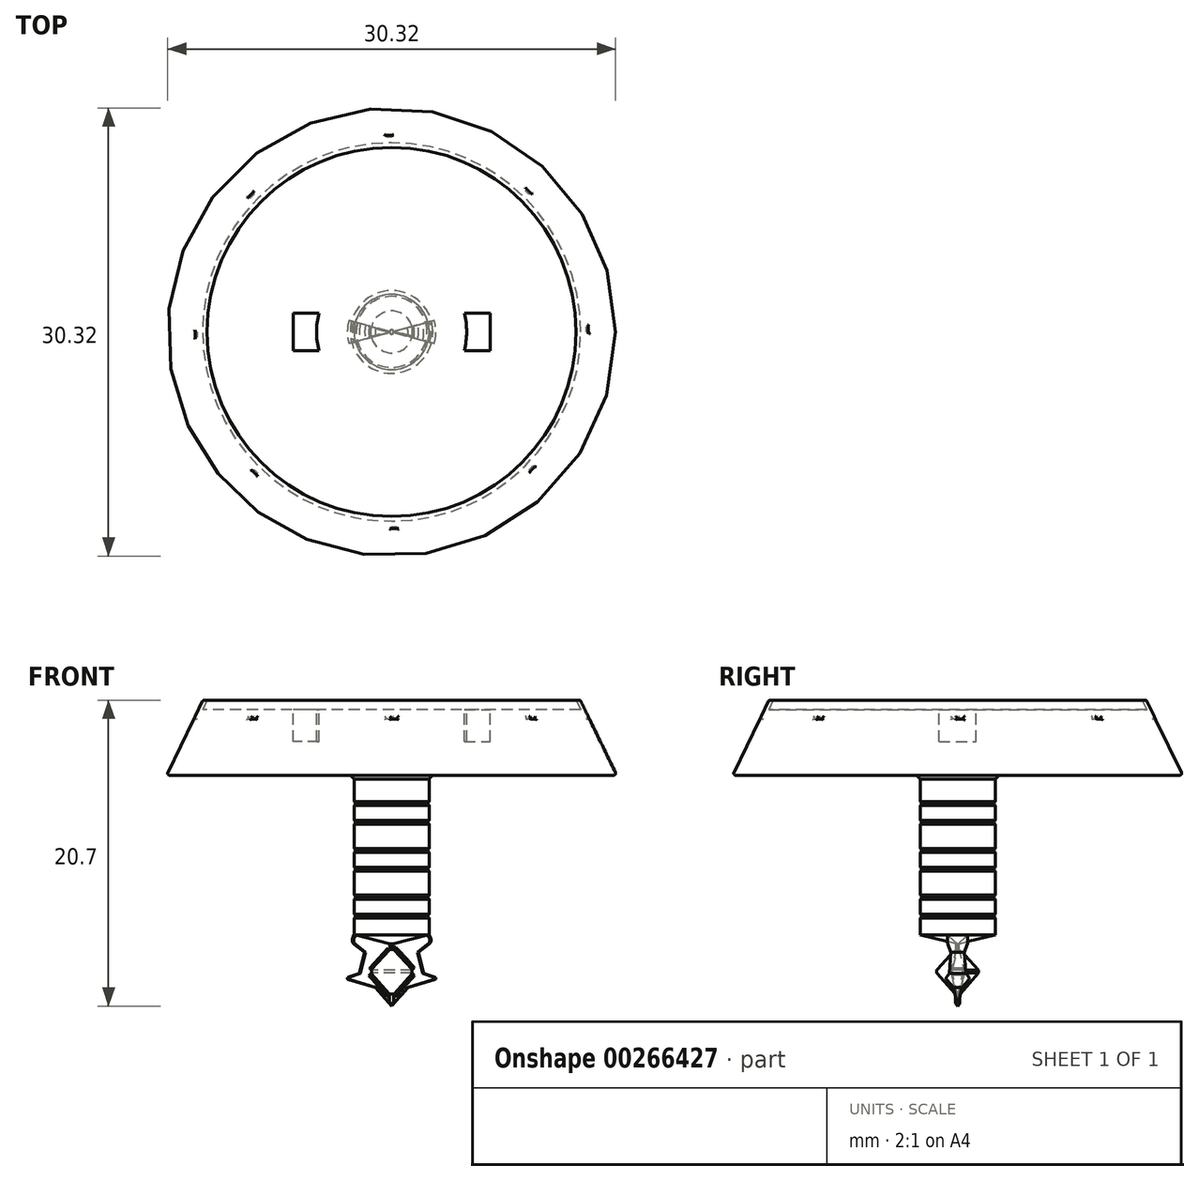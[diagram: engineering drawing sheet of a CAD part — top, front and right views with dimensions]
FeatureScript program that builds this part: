
annotation { "Feature Type Name" : "Feature", "Feature Type Description" : "" }
export const myFeature = defineFeature(function(context is Context, id is Id, definition is map)
    precondition{}
    {
        {
            var Q0;
            Q0=qCreatedBy(makeId("Top.planeOp"),FACE);
            var sketch = newSketch(context, id + "F0", { "sketchPlane" : qUnion([Q0])});
            skLineSegment(sketch, "E0", {"start": v(-1.59, 0) * mm, "end": v(-1.59, 1.27) * mm});
            skLineSegment(sketch, "E1", {"start": v(1.59, 0) * mm, "end": v(1.59, 1.27) * mm});
            skLineSegment(sketch, "E2", {"start": v(1.59, 0) * mm, "end": v(1.59, -1.27) * mm});
            skLineSegment(sketch, "E3", {"start": v(-1.59, 0) * mm, "end": v(-1.59, -1.27) * mm});
            skLineSegment(sketch, "E4.bottom", {"start": v(1.59, -1.27) * mm, "end": v(6.67, -1.27) * mm});
            skLineSegment(sketch, "E4.top", {"start": v(1.59, 1.26) * mm, "end": v(6.67, 1.26) * mm});
            skLineSegment(sketch, "E4.left", {"start": v(1.59, -1.27) * mm, "end": v(1.59, 1.26) * mm});
            skLineSegment(sketch, "E4.right", {"start": v(6.67, -1.27) * mm, "end": v(6.67, 1.26) * mm});
            skLineSegment(sketch, "E5.bottom", {"start": v(-1.59, -1.27) * mm, "end": v(-6.67, -1.27) * mm});
            skLineSegment(sketch, "E5.top", {"start": v(-1.59, 1.26) * mm, "end": v(-6.67, 1.26) * mm});
            skLineSegment(sketch, "E5.left", {"start": v(-1.59, -1.27) * mm, "end": v(-1.59, 1.26) * mm});
            skLineSegment(sketch, "E5.right", {"start": v(-6.67, -1.27) * mm, "end": v(-6.67, 1.26) * mm});
            skCircle(sketch, "E6", {"center": v(0, 0) * mm, "radius": 5.08 * mm});
            skCircle(sketch, "E7", {"center": v(0, 0) * mm, "radius": 12.7 * mm});
            skLineSegment(sketch, "E8", {"start": v(0, 0) * mm, "end": v(-1.59, 0) * mm});
            skLineSegment(sketch, "E9", {"start": v(0, 0) * mm, "end": v(1.59, 0) * mm});
            skSolve(sketch);
        }
        {
            var Q0;
            Q0=qCreatedBy(makeId("Front.planeOp"),FACE);
            var sketch = newSketch(context, id + "F1", { "sketchPlane" : qUnion([Q0])});
            skLineSegment(sketch, "E10", {"start": v(0, 0) * mm, "end": v(0, -1.27) * mm});
            skLineSegment(sketch, "E11", {"start": v(0, -1.27) * mm, "end": v(0, -3.81) * mm});
            skLineSegment(sketch, "E12", {"start": v(0, -3.81) * mm, "end": v(0, -5.08) * mm});
            skLineSegment(sketch, "E13", {"start": v(0, -5.08) * mm, "end": v(0, -6.99) * mm});
            skLineSegment(sketch, "E14", {"start": v(0, -14.6) * mm, "end": v(0, -16.51) * mm});
            skLineSegment(sketch, "E15", {"start": v(0.24, -16.76) * mm, "end": v(1.54, -18.15) * mm});
            skLineSegment(sketch, "E16", {"start": v(1.54, -18.58) * mm, "end": v(0.26, -20.03) * mm});
            skLineSegment(sketch, "E17", {"start": v(0, -16.98) * mm, "end": v(0, -19.74) * mm});
            skLineSegment(sketch, "E18", {"start": v(2.18, -18.5) * mm, "end": v(3.18, -18.84) * mm});
            skLineSegment(sketch, "E19", {"start": v(0.12, -16.48) * mm, "end": v(2.54, -15.9) * mm});
            skLineSegment(sketch, "E20", {"start": v(0.12, -16.5) * mm, "end": v(2.79, -16.33) * mm});
            skLineSegment(sketch, "E21", {"start": v(0.12, -16.55) * mm, "end": v(1.82, -17.06) * mm});
            skLineSegment(sketch, "E22", {"start": v(1.82, -17.06) * mm, "end": v(2.79, -16.33) * mm});
            skLineSegment(sketch, "E23", {"start": v(1.82, -17.06) * mm, "end": v(2.18, -18.5) * mm});
            skLineSegment(sketch, "E24", {"start": v(0, -5.08) * mm, "end": v(14.96, -5.08) * mm});
            skLineSegment(sketch, "E25", {"start": v(12.49, 0) * mm, "end": v(0, 0) * mm});
            skLineSegment(sketch, "E26", {"start": v(0, -1.27) * mm, "end": v(13.1, -1.27) * mm});
            skLineSegment(sketch, "E27", {"start": v(0, -3.81) * mm, "end": v(14.34, -3.81) * mm});
            skLineSegment(sketch, "E28.MirrorCS", {"start": v(0, -1.27) * mm, "end": v(-13.39, -1.27) * mm});
            skLineSegment(sketch, "E29.MirrorCS", {"start": v(0, -3.81) * mm, "end": v(-14.62, -3.81) * mm});
            skLineSegment(sketch, "E30.MirrorCS", {"start": v(0, -5.08) * mm, "end": v(-15.24, -5.08) * mm});
            skLineSegment(sketch, "E31.MirrorCS", {"start": v(-15.24, -5.08) * mm, "end": v(-12.77, 0) * mm});
            skLineSegment(sketch, "E32.MirrorCS", {"start": v(-12.77, 0) * mm, "end": v(0, 0) * mm});
            skLineSegment(sketch, "E33", {"start": v(0, 0) * mm, "end": v(2.54, 0) * mm});
            skLineSegment(sketch, "E34", {"start": v(2.54, -15.9) * mm, "end": v(2.79, -16.33) * mm});
            skLineSegment(sketch, "E35", {"start": v(0, -6.99) * mm, "end": v(2.4, -6.99) * mm});
            skLineSegment(sketch, "E36", {"start": v(0, -10.16) * mm, "end": v(2.4, -10.16) * mm});
            skLineSegment(sketch, "E37", {"start": v(0, -11.43) * mm, "end": v(2.4, -11.43) * mm});
            skLineSegment(sketch, "E38", {"start": v(0, -13.33) * mm, "end": v(2.4, -13.33) * mm});
            skLineSegment(sketch, "E39", {"start": v(0, -14.6) * mm, "end": v(2.4, -14.6) * mm});
            skLineSegment(sketch, "E40", {"start": v(2.54, -15.9) * mm, "end": v(2.54, -14.73) * mm});
            skLineSegment(sketch, "E41", {"start": v(2.54, -14.48) * mm, "end": v(2.54, -13.46) * mm});
            skLineSegment(sketch, "E42", {"start": v(2.54, -13.2) * mm, "end": v(2.54, -11.56) * mm});
            skLineSegment(sketch, "E43", {"start": v(2.54, -11.3) * mm, "end": v(2.54, -10.29) * mm});
            skLineSegment(sketch, "E44", {"start": v(2.54, -10.03) * mm, "end": v(2.54, -8.38) * mm});
            skLineSegment(sketch, "E45", {"start": v(2.54, -8.13) * mm, "end": v(2.54, -7.11) * mm});
            skLineSegment(sketch, "E46", {"start": v(2.54, -6.86) * mm, "end": v(2.54, -5.33) * mm});
            skLineSegment(sketch, "E47.MirrorCS", {"start": v(-0.12, -16.48) * mm, "end": v(-2.54, -15.9) * mm});
            skLineSegment(sketch, "E48.MirrorCS", {"start": v(-0.12, -16.5) * mm, "end": v(-2.79, -16.33) * mm});
            skLineSegment(sketch, "E49.MirrorCS", {"start": v(-0.12, -16.55) * mm, "end": v(-1.82, -17.06) * mm});
            skLineSegment(sketch, "E50.MirrorCS", {"start": v(-1.82, -17.06) * mm, "end": v(-2.79, -16.33) * mm});
            skLineSegment(sketch, "E51.MirrorCS", {"start": v(-2.54, -15.9) * mm, "end": v(-2.79, -16.33) * mm});
            skLineSegment(sketch, "E52.0", {"start": v(1.11, -19.45) * mm, "end": v(0, -20.7) * mm});
            skLineSegment(sketch, "E53", {"start": v(3.18, -18.84) * mm, "end": v(1.11, -19.45) * mm});
            skLineSegment(sketch, "E54", {"start": v(0, -5.08) * mm, "end": v(0, -5.33) * mm});
            skLineSegment(sketch, "E55", {"start": v(0, -5.33) * mm, "end": v(2.54, -5.33) * mm});
            skLineSegment(sketch, "E56", {"start": v(0, -6.86) * mm, "end": v(2.54, -6.86) * mm});
            skLineSegment(sketch, "E57", {"start": v(0, -7.11) * mm, "end": v(2.54, -7.11) * mm});
            skLineSegment(sketch, "E58", {"start": v(0, -8.13) * mm, "end": v(2.54, -8.13) * mm});
            skLineSegment(sketch, "E59", {"start": v(0, -8.38) * mm, "end": v(2.54, -8.38) * mm});
            skLineSegment(sketch, "E60", {"start": v(0, -10.03) * mm, "end": v(2.54, -10.03) * mm});
            skLineSegment(sketch, "E61", {"start": v(0, -10.29) * mm, "end": v(2.54, -10.29) * mm});
            skLineSegment(sketch, "E62", {"start": v(0, -11.3) * mm, "end": v(2.54, -11.3) * mm});
            skLineSegment(sketch, "E63", {"start": v(0, -11.56) * mm, "end": v(2.54, -11.56) * mm});
            skLineSegment(sketch, "E64", {"start": v(0, -13.2) * mm, "end": v(2.54, -13.2) * mm});
            skLineSegment(sketch, "E65", {"start": v(0, -13.46) * mm, "end": v(2.54, -13.46) * mm});
            skLineSegment(sketch, "E66", {"start": v(0, -14.48) * mm, "end": v(2.54, -14.48) * mm});
            skLineSegment(sketch, "E67", {"start": v(0, -14.73) * mm, "end": v(2.54, -14.73) * mm});
            skLineSegment(sketch, "E68", {"start": v(0, -5.08) * mm, "end": v(2.8, -5.08) * mm});
            skLineSegment(sketch, "E69", {"start": v(2.54, -5.33) * mm, "end": v(2.8, -5.08) * mm});
            skPoint(sketch, "E70.orphan", {"position": v(2.54, -5.08) * mm});
            skLineSegment(sketch, "E71", {"start": v(2.4, -6.99) * mm, "end": v(2.54, -6.86) * mm});
            skLineSegment(sketch, "E72", {"start": v(2.54, -7.11) * mm, "end": v(2.4, -6.98) * mm});
            skLineSegment(sketch, "E73", {"start": v(2.4, -8.26) * mm, "end": v(2.54, -8.13) * mm});
            skLineSegment(sketch, "E74", {"start": v(2.4, -8.26) * mm, "end": v(2.54, -8.38) * mm});
            skLineSegment(sketch, "E75", {"start": v(2.4, -10.16) * mm, "end": v(2.54, -10.03) * mm});
            skLineSegment(sketch, "E76", {"start": v(2.54, -10.29) * mm, "end": v(2.4, -10.16) * mm});
            skLineSegment(sketch, "E77", {"start": v(2.4, -11.43) * mm, "end": v(2.54, -11.3) * mm});
            skLineSegment(sketch, "E78", {"start": v(2.54, -11.56) * mm, "end": v(2.4, -11.43) * mm});
            skLineSegment(sketch, "E79", {"start": v(2.4, -13.34) * mm, "end": v(2.54, -13.2) * mm});
            skLineSegment(sketch, "E80", {"start": v(2.54, -13.46) * mm, "end": v(2.4, -13.33) * mm});
            skLineSegment(sketch, "E81", {"start": v(2.4, -14.6) * mm, "end": v(2.54, -14.48) * mm});
            skLineSegment(sketch, "E82", {"start": v(2.54, -14.73) * mm, "end": v(2.4, -14.6) * mm});
            skPoint(sketch, "E83.orphan", {"position": v(2.54, -6.99) * mm});
            skPoint(sketch, "E84.orphan", {"position": v(2.54, -8.26) * mm});
            skPoint(sketch, "E85.start.orphan", {"position": v(2.54, -10.16) * mm});
            skPoint(sketch, "E86.start.orphan", {"position": v(2.54, -11.43) * mm});
            skPoint(sketch, "E87.orphan", {"position": v(2.54, -14.6) * mm});
            skPoint(sketch, "E88.orphan", {"position": v(2.54, -13.33) * mm});
            skLineSegment(sketch, "E89", {"start": v(0, -6.86) * mm, "end": v(0, -14.73) * mm});
            skLineSegment(sketch, "E90.MirrorCS", {"start": v(0, -14.73) * mm, "end": v(-2.54, -14.73) * mm});
            skLineSegment(sketch, "E91.MirrorCS", {"start": v(-2.54, -15.9) * mm, "end": v(-2.54, -14.73) * mm});
            skLineSegment(sketch, "E92.MirrorCS", {"start": v(-2.54, -14.73) * mm, "end": v(-2.4, -14.6) * mm});
            skLineSegment(sketch, "E93.MirrorCS", {"start": v(-2.4, -10.16) * mm, "end": v(-2.54, -10.03) * mm});
            skLineSegment(sketch, "E94.MirrorCS", {"start": v(-2.4, -11.43) * mm, "end": v(-2.54, -11.3) * mm});
            skLineSegment(sketch, "E95.MirrorCS", {"start": v(-2.54, -11.56) * mm, "end": v(-2.4, -11.43) * mm});
            skLineSegment(sketch, "E96.MirrorCS", {"start": v(-2.4, -14.6) * mm, "end": v(-2.54, -14.48) * mm});
            skLineSegment(sketch, "E97.MirrorCS", {"start": v(-2.4, -8.26) * mm, "end": v(-2.54, -8.38) * mm});
            skLineSegment(sketch, "E98.MirrorCS", {"start": v(-2.4, -6.99) * mm, "end": v(-2.54, -6.86) * mm});
            skLineSegment(sketch, "E99.MirrorCS", {"start": v(-2.54, -13.46) * mm, "end": v(-2.4, -13.33) * mm});
            skLineSegment(sketch, "E100.MirrorCS", {"start": v(-2.4, -8.26) * mm, "end": v(-2.54, -8.13) * mm});
            skLineSegment(sketch, "E101.MirrorCS", {"start": v(-2.54, -7.11) * mm, "end": v(-2.4, -6.98) * mm});
            skLineSegment(sketch, "E102.MirrorCS", {"start": v(-2.4, -13.34) * mm, "end": v(-2.54, -13.2) * mm});
            skLineSegment(sketch, "E103.MirrorCS", {"start": v(-2.54, -10.29) * mm, "end": v(-2.4, -10.16) * mm});
            skLineSegment(sketch, "E104.MirrorCS", {"start": v(-2.54, -5.33) * mm, "end": v(-2.8, -5.08) * mm});
            skLineSegment(sketch, "E105.MirrorCS", {"start": v(0, -7.11) * mm, "end": v(-2.54, -7.11) * mm});
            skPoint(sketch, "E106.MirrorP", {"position": v(-2.54, -10.16) * mm});
            skLineSegment(sketch, "E107.MirrorCS", {"start": v(-2.54, -11.3) * mm, "end": v(-2.54, -10.29) * mm});
            skLineSegment(sketch, "E108.MirrorCS", {"start": v(0, -10.03) * mm, "end": v(-2.54, -10.03) * mm});
            skPoint(sketch, "E109.MirrorP", {"position": v(-2.54, -6.99) * mm});
            skLineSegment(sketch, "E110.MirrorCS", {"start": v(0, -8.38) * mm, "end": v(-2.54, -8.38) * mm});
            skLineSegment(sketch, "E111.MirrorCS", {"start": v(0, -11.3) * mm, "end": v(-2.54, -11.3) * mm});
            skLineSegment(sketch, "E112.MirrorCS", {"start": v(0, -6.86) * mm, "end": v(-2.54, -6.86) * mm});
            skLineSegment(sketch, "E113.MirrorCS", {"start": v(0, -13.46) * mm, "end": v(-2.54, -13.46) * mm});
            skLineSegment(sketch, "E114.MirrorCS", {"start": v(0, -5.08) * mm, "end": v(-2.8, -5.08) * mm});
            skLineSegment(sketch, "E115.MirrorCS", {"start": v(0, -14.48) * mm, "end": v(-2.54, -14.48) * mm});
            skLineSegment(sketch, "E116.MirrorCS", {"start": v(0, -10.16) * mm, "end": v(-2.4, -10.16) * mm});
            skPoint(sketch, "E117.MirrorP", {"position": v(-2.54, -11.43) * mm});
            skPoint(sketch, "E118.MirrorP", {"position": v(-2.54, -13.33) * mm});
            skPoint(sketch, "E119.MirrorP", {"position": v(-2.54, -5.08) * mm});
            skLineSegment(sketch, "E120.MirrorCS", {"start": v(0, -13.2) * mm, "end": v(-2.54, -13.2) * mm});
            skLineSegment(sketch, "E121.MirrorCS", {"start": v(-2.54, -10.03) * mm, "end": v(-2.54, -8.38) * mm});
            skPoint(sketch, "E122.MirrorP", {"position": v(-2.54, -8.26) * mm});
            skLineSegment(sketch, "E123.MirrorCS", {"start": v(0, -8.13) * mm, "end": v(-2.54, -8.13) * mm});
            skPoint(sketch, "E124.MirrorP", {"position": v(-2.54, -14.6) * mm});
            skLineSegment(sketch, "E125.MirrorCS", {"start": v(0, -14.6) * mm, "end": v(-2.4, -14.6) * mm});
            skLineSegment(sketch, "E126.MirrorCS", {"start": v(-2.54, -6.86) * mm, "end": v(-2.54, -5.33) * mm});
            skLineSegment(sketch, "E127.MirrorCS", {"start": v(0, -11.56) * mm, "end": v(-2.54, -11.56) * mm});
            skLineSegment(sketch, "E128.MirrorCS", {"start": v(0, -13.33) * mm, "end": v(-2.4, -13.33) * mm});
            skLineSegment(sketch, "E129.MirrorCS", {"start": v(0, -5.33) * mm, "end": v(-2.54, -5.33) * mm});
            skLineSegment(sketch, "E130.MirrorCS", {"start": v(-2.54, -14.48) * mm, "end": v(-2.54, -13.46) * mm});
            skLineSegment(sketch, "E131.MirrorCS", {"start": v(0, -11.43) * mm, "end": v(-2.4, -11.43) * mm});
            skLineSegment(sketch, "E132.MirrorCS", {"start": v(0, -10.29) * mm, "end": v(-2.54, -10.29) * mm});
            skLineSegment(sketch, "E133.MirrorCS", {"start": v(0, -6.99) * mm, "end": v(-2.4, -6.99) * mm});
            skLineSegment(sketch, "E134.MirrorCS", {"start": v(-2.54, -8.13) * mm, "end": v(-2.54, -7.11) * mm});
            skLineSegment(sketch, "E135.MirrorCS", {"start": v(-2.54, -13.2) * mm, "end": v(-2.54, -11.56) * mm});
            skLineSegment(sketch, "E136", {"start": v(-2.4, -8.26) * mm, "end": v(2.4, -8.26) * mm});
            skLineSegment(sketch, "E137", {"start": v(0, 0) * mm, "end": v(0, -0.64) * mm});
            skLineSegment(sketch, "E138", {"start": v(0, -0.64) * mm, "end": v(12.8, -0.64) * mm});
            skLineSegment(sketch, "E139", {"start": v(0, -0.64) * mm, "end": v(-13.08, -0.64) * mm});
            skLineSegment(sketch, "E140.0", {"start": v(-14.96, -5.08) * mm, "end": v(-12.49, 0) * mm});
            skLineSegment(sketch, "E141", {"start": v(0.24, -16.76) * mm, "end": v(0.12, -16.87) * mm});
            skLineSegment(sketch, "E142", {"start": v(0.26, -20.03) * mm, "end": v(0.15, -19.9) * mm});
            skLineSegment(sketch, "E143", {"start": v(1.42, -18.47) * mm, "end": v(1.54, -18.58) * mm});
            skLineSegment(sketch, "E144.MirrorCS", {"start": v(1.42, -18.26) * mm, "end": v(1.54, -18.15) * mm});
            skLineSegment(sketch, "E145", {"start": v(1.42, -18.47) * mm, "end": v(0.15, -19.9) * mm});
            skLineSegment(sketch, "E146", {"start": v(1.42, -18.26) * mm, "end": v(0.12, -16.87) * mm});
            skPoint(sketch, "E146.endSnap0", {"position": v(0.12, -16.87) * mm});
            skLineSegment(sketch, "E147", {"start": v(0, -0.64) * mm, "end": v(0, -3.81) * mm});
            skLineSegment(sketch, "E148.MirrorCS", {"start": v(14.96, -5.08) * mm, "end": v(12.49, 0) * mm});
            skPoint(sketch, "E149.orphan", {"position": v(12.77, 0) * mm});
            skPoint(sketch, "E150.orphan", {"position": v(13.39, -1.27) * mm});
            skPoint(sketch, "E151.orphan", {"position": v(14.62, -3.81) * mm});
            skPoint(sketch, "E152.orphan", {"position": v(15.24, -5.08) * mm});
            skLineSegment(sketch, "E153", {"start": v(1.42, -18.47) * mm, "end": v(1.42, -18.26) * mm});
            skLineSegment(sketch, "E154", {"start": v(0, -16.98) * mm, "end": v(0, -16.51) * mm});
            skLineSegment(sketch, "E155", {"start": v(0, -19.74) * mm, "end": v(0, -20.7) * mm});
            skLineSegment(sketch, "E156.MirrorCS", {"start": v(-1.42, -18.26) * mm, "end": v(-0.12, -16.87) * mm});
            skLineSegment(sketch, "E157.MirrorCS", {"start": v(-0.24, -16.76) * mm, "end": v(-0.12, -16.87) * mm});
            skLineSegment(sketch, "E158.MirrorCS", {"start": v(-0.24, -16.76) * mm, "end": v(-1.54, -18.15) * mm});
            skLineSegment(sketch, "E159.MirrorCS", {"start": v(-1.42, -18.47) * mm, "end": v(-1.54, -18.58) * mm});
            skLineSegment(sketch, "E160.MirrorCS", {"start": v(-1.42, -18.26) * mm, "end": v(-1.54, -18.15) * mm});
            skLineSegment(sketch, "E161.MirrorCS", {"start": v(-1.42, -18.47) * mm, "end": v(-0.15, -19.9) * mm});
            skLineSegment(sketch, "E162.MirrorCS", {"start": v(-1.11, -19.45) * mm, "end": v(0, -20.7) * mm});
            skLineSegment(sketch, "E163.MirrorCS", {"start": v(-1.42, -18.47) * mm, "end": v(-1.42, -18.26) * mm});
            skLineSegment(sketch, "E164.MirrorCS", {"start": v(-3.18, -18.84) * mm, "end": v(-1.11, -19.45) * mm});
            skLineSegment(sketch, "E165.MirrorCS", {"start": v(-1.82, -17.06) * mm, "end": v(-2.18, -18.5) * mm});
            skLineSegment(sketch, "E166.MirrorCS", {"start": v(-2.18, -18.5) * mm, "end": v(-3.18, -18.84) * mm});
            skLineSegment(sketch, "E167.MirrorCS", {"start": v(-1.54, -18.58) * mm, "end": v(-0.26, -20.03) * mm});
            skLineSegment(sketch, "E168.MirrorCS", {"start": v(-0.26, -20.03) * mm, "end": v(-0.15, -19.9) * mm});
            skPoint(sketch, "E169.orphan", {"position": v(-0.12, -16.86) * mm});
            skPoint(sketch, "E170.orphan", {"position": v(0.12, -16.86) * mm});
            skLineSegment(sketch, "E171", {"start": v(0.12, -16.87) * mm, "end": v(0.12, -16.48) * mm});
            skLineSegment(sketch, "E172", {"start": v(0.12, -16.48) * mm, "end": v(-0.12, -16.48) * mm});
            skLineSegment(sketch, "E173", {"start": v(-0.12, -16.48) * mm, "end": v(-0.12, -16.87) * mm});
            skPoint(sketch, "E174.orphan", {"position": v(0, -16.98) * mm});
            skLineSegment(sketch, "E175", {"start": v(-0.15, -19.9) * mm, "end": v(-0.15, -20.54) * mm});
            skLineSegment(sketch, "E176", {"start": v(0.15, -20.54) * mm, "end": v(0.15, -19.9) * mm});
            skPoint(sketch, "E177.orphan", {"position": v(0, -19.74) * mm});
            skSolve(sketch);
        }
        {
            var Q0;
            {var subQ0=sQuery(id+"F1.wireOp",EDGE,"E137");Q0=makeQuery(id+"F1.imprint","IMPRINT",FACE,{"disambiguationData":[TD([[makeQuery(id+"F1.imprint","IMPRINT",EDGE,{"derivedFrom":subQ0}),-1.0]])]});}
            var Q1;
            {var subQ0=sQuery(id+"F1.wireOp",EDGE,"E28.MirrorCS");var subQ1=sQuery(id+"F1.wireOp",EDGE,"E140.0");var subQ2=makeQuery(id+"F1.imprint","INTERSECT",VERTEX,{"derivedFrom":[subQ1,subQ0]});Q1=makeQuery(id+"F1.imprint","IMPRINT",FACE,{"disambiguationData":[TD([[makeQuery(id+"F1.imprint","IMPRINT",EDGE,{"disambiguationData":[TD([[subQ2,-1.0]])],"derivedFrom":subQ1}),-1.0]])]});}
            var Q2;
            {var subQ0=sQuery(id+"F1.wireOp",EDGE,"E29.MirrorCS");var subQ1=sQuery(id+"F1.wireOp",EDGE,"E140.0");var subQ2=makeQuery(id+"F1.imprint","INTERSECT",VERTEX,{"derivedFrom":[subQ1,subQ0]});Q2=makeQuery(id+"F1.imprint","IMPRINT",FACE,{"disambiguationData":[TD([[makeQuery(id+"F1.imprint","IMPRINT",EDGE,{"disambiguationData":[TD([[subQ2,-1.0]])],"derivedFrom":subQ1}),-1.0]])]});}
            var Q3;
            {var subQ6=sQuery(id+"F1.wireOp",EDGE,"E12");Q3=makeQuery(id+"F1.imprint","IMPRINT",FACE,{"disambiguationData":[TD([[makeQuery(id+"F1.imprint","IMPRINT",EDGE,{"derivedFrom":subQ6}),-1.0]])]});}
            var Q4;
            Q4=makeQuery(id+"F1.imprint","IMPRINT",FACE,{"disambiguationData":[TD([[makeQuery(id+"F1.imprint","IMPRINT",EDGE,{"derivedFrom":sQuery(id+"F1.wireOp",EDGE,"E104.MirrorCS")}),-1.0]])]});
            var Q5;
            {var subQ2=sQuery(id+"F1.wireOp",EDGE,"E112.MirrorCS");Q5=makeQuery(id+"F1.imprint","IMPRINT",FACE,{"disambiguationData":[TD([[makeQuery(id+"F1.imprint","IMPRINT",EDGE,{"derivedFrom":subQ2}),-1.0]])]});}
            var Q6;
            Q6=makeQuery(id+"F1.imprint","IMPRINT",FACE,{"disambiguationData":[TD([[makeQuery(id+"F1.imprint","IMPRINT",EDGE,{"derivedFrom":sQuery(id+"F1.wireOp",EDGE,"E98.MirrorCS")}),-1.0]])]});
            var Q7;
            Q7=makeQuery(id+"F1.imprint","IMPRINT",FACE,{"disambiguationData":[TD([[makeQuery(id+"F1.imprint","IMPRINT",EDGE,{"derivedFrom":sQuery(id+"F1.wireOp",EDGE,"E101.MirrorCS")}),-1.0]])]});
            var Q8;
            {var subQ0=sQuery(id+"F1.wireOp",EDGE,"E105.MirrorCS");Q8=makeQuery(id+"F1.imprint","IMPRINT",FACE,{"disambiguationData":[TD([[makeQuery(id+"F1.imprint","IMPRINT",EDGE,{"derivedFrom":subQ0}),1.0]])]});}
            var Q9;
            {var subQ4=sQuery(id+"F1.wireOp",EDGE,"E100.MirrorCS");Q9=makeQuery(id+"F1.imprint","IMPRINT",FACE,{"disambiguationData":[TD([[makeQuery(id+"F1.imprint","IMPRINT",EDGE,{"derivedFrom":subQ4}),-1.0]])]});}
            var Q10;
            {var subQ2=sQuery(id+"F1.wireOp",EDGE,"E108.MirrorCS");Q10=makeQuery(id+"F1.imprint","IMPRINT",FACE,{"disambiguationData":[TD([[makeQuery(id+"F1.imprint","IMPRINT",EDGE,{"derivedFrom":subQ2}),-1.0]])]});}
            var Q11;
            {var subQ4=sQuery(id+"F1.wireOp",EDGE,"E97.MirrorCS");Q11=makeQuery(id+"F1.imprint","IMPRINT",FACE,{"disambiguationData":[TD([[makeQuery(id+"F1.imprint","IMPRINT",EDGE,{"derivedFrom":subQ4}),1.0]])]});}
            var Q12;
            Q12=makeQuery(id+"F1.imprint","IMPRINT",FACE,{"disambiguationData":[TD([[makeQuery(id+"F1.imprint","IMPRINT",EDGE,{"derivedFrom":sQuery(id+"F1.wireOp",EDGE,"E103.MirrorCS")}),-1.0]])]});
            var Q13;
            Q13=makeQuery(id+"F1.imprint","IMPRINT",FACE,{"disambiguationData":[TD([[makeQuery(id+"F1.imprint","IMPRINT",EDGE,{"derivedFrom":sQuery(id+"F1.wireOp",EDGE,"E93.MirrorCS")}),-1.0]])]});
            var Q14;
            Q14=makeQuery(id+"F1.imprint","IMPRINT",FACE,{"disambiguationData":[TD([[makeQuery(id+"F1.imprint","IMPRINT",EDGE,{"derivedFrom":sQuery(id+"F1.wireOp",EDGE,"E107.MirrorCS")}),-1.0]])]});
            var Q15;
            Q15=makeQuery(id+"F1.imprint","IMPRINT",FACE,{"disambiguationData":[TD([[makeQuery(id+"F1.imprint","IMPRINT",EDGE,{"derivedFrom":sQuery(id+"F1.wireOp",EDGE,"E94.MirrorCS")}),-1.0]])]});
            var Q16;
            Q16=makeQuery(id+"F1.imprint","IMPRINT",FACE,{"disambiguationData":[TD([[makeQuery(id+"F1.imprint","IMPRINT",EDGE,{"derivedFrom":sQuery(id+"F1.wireOp",EDGE,"E95.MirrorCS")}),-1.0]])]});
            var Q17;
            {var subQ2=sQuery(id+"F1.wireOp",EDGE,"E120.MirrorCS");Q17=makeQuery(id+"F1.imprint","IMPRINT",FACE,{"disambiguationData":[TD([[makeQuery(id+"F1.imprint","IMPRINT",EDGE,{"derivedFrom":subQ2}),-1.0]])]});}
            var Q18;
            Q18=makeQuery(id+"F1.imprint","IMPRINT",FACE,{"disambiguationData":[TD([[makeQuery(id+"F1.imprint","IMPRINT",EDGE,{"derivedFrom":sQuery(id+"F1.wireOp",EDGE,"E102.MirrorCS")}),-1.0]])]});
            var Q19;
            Q19=makeQuery(id+"F1.imprint","IMPRINT",FACE,{"disambiguationData":[TD([[makeQuery(id+"F1.imprint","IMPRINT",EDGE,{"derivedFrom":sQuery(id+"F1.wireOp",EDGE,"E99.MirrorCS")}),-1.0]])]});
            var Q20;
            {var subQ0=sQuery(id+"F1.wireOp",EDGE,"E113.MirrorCS");Q20=makeQuery(id+"F1.imprint","IMPRINT",FACE,{"disambiguationData":[TD([[makeQuery(id+"F1.imprint","IMPRINT",EDGE,{"derivedFrom":subQ0}),1.0]])]});}
            var Q21;
            Q21=makeQuery(id+"F1.imprint","IMPRINT",FACE,{"disambiguationData":[TD([[makeQuery(id+"F1.imprint","IMPRINT",EDGE,{"derivedFrom":sQuery(id+"F1.wireOp",EDGE,"E96.MirrorCS")}),-1.0]])]});
            var Q22;
            {var subQ0=sQuery(id+"F1.wireOp",EDGE,"E90.MirrorCS");Q22=makeQuery(id+"F1.imprint","IMPRINT",FACE,{"disambiguationData":[TD([[makeQuery(id+"F1.imprint","IMPRINT",EDGE,{"derivedFrom":subQ0}),-1.0]])]});}
            var Q23;
            {var subQ0=sQuery(id+"F1.wireOp",EDGE,"E47.MirrorCS");Q23=makeQuery(id+"F1.imprint","IMPRINT",FACE,{"disambiguationData":[TD([[makeQuery(id+"F1.imprint","IMPRINT",EDGE,{"derivedFrom":subQ0}),-1.0]])]});}
            var Q24;
            Q24=sQuery(id+"F1.wireOp",EDGE,"E14");
            revolve(context, id + "F2", {"entities" : qUnion([Q0, Q1, Q2, Q3, Q4, Q5, Q6, Q7, Q8, Q9, Q10, Q11, Q12, Q13, Q14, Q15, Q16, Q17, Q18, Q19, Q20, Q21, Q22, Q23]), "axis" : qUnion([Q24]), "revolveType" : RevolveType.FULL});
        }
        {
            var Q0;
            {var subQ2=sQuery(id+"F1.wireOp",EDGE,"E17");Q0=makeQuery(id+"F1.imprint","IMPRINT",FACE,{"disambiguationData":[TD([[makeQuery(id+"F1.imprint","IMPRINT",EDGE,{"derivedFrom":subQ2}),1.0]])]});}
            var Q1;
            Q1=sQuery(id+"F1.wireOp",EDGE,"E17");
            revolve(context, id + "F3", {"entities" : qUnion([Q0]), "axis" : qUnion([Q1]), "revolveType" : RevolveType.FULL});
        }
        {
            var Q0;
            {var subQ0=sQuery(id+"F1.wireOp",EDGE,"E32.MirrorCS");var subQ1=sQuery(id+"F1.wireOp",EDGE,"E31.MirrorCS");var subQ2=makeQuery(id+"F1.imprint","INTERSECT",VERTEX,{"derivedFrom":[subQ1,subQ0]});Q0=makeQuery(id+"F1.imprint","IMPRINT",FACE,{"disambiguationData":[TD([[makeQuery(id+"F1.imprint","IMPRINT",EDGE,{"disambiguationData":[TD([[subQ2,1.0]])],"derivedFrom":subQ1}),-1.0]])]});}
            var Q1;
            Q1=sQuery(id+"F1.wireOp",EDGE,"E137");
            revolve(context, id + "F4", {"operationType" : NewBodyOperationType.ADD, "entities" : qUnion([Q0]), "axis" : qUnion([Q1]), "revolveType" : RevolveType.FULL});
        }
        {
            var Q0;
            {var subQ0=sQuery(id+"F1.wireOp",EDGE,"E28.MirrorCS");var subQ1=sQuery(id+"F1.wireOp",EDGE,"E31.MirrorCS");var subQ2=makeQuery(id+"F1.imprint","INTERSECT",VERTEX,{"derivedFrom":[subQ1,subQ0]});Q0=makeQuery(id+"F1.imprint","IMPRINT",FACE,{"disambiguationData":[TD([[makeQuery(id+"F1.imprint","IMPRINT",EDGE,{"disambiguationData":[TD([[subQ2,-1.0]])],"derivedFrom":subQ1}),-1.0]])]});}
            var Q1;
            Q1=sQuery(id+"F1.wireOp",EDGE,"E10");
            revolve(context, id + "F5", {"entities" : qUnion([Q0]), "axis" : qUnion([Q1]), "revolveType" : RevolveType.SYMMETRIC, "angle" : 43.5 * degree});
        }
        {
            var Q0;
            {var subQ0=sQuery(id+"F1.wireOp",EDGE,"E29.MirrorCS");var subQ1=sQuery(id+"F1.wireOp",EDGE,"E31.MirrorCS");var subQ2=makeQuery(id+"F1.imprint","INTERSECT",VERTEX,{"derivedFrom":[subQ1,subQ0]});Q0=makeQuery(id+"F1.imprint","IMPRINT",FACE,{"disambiguationData":[TD([[makeQuery(id+"F1.imprint","IMPRINT",EDGE,{"disambiguationData":[TD([[subQ2,-1.0]])],"derivedFrom":subQ1}),-1.0]])]});}
            var Q1;
            Q1=sQuery(id+"F1.wireOp",EDGE,"E11");
            revolve(context, id + "F6", {"entities" : qUnion([Q0]), "axis" : qUnion([Q1]), "revolveType" : RevolveType.ONE_DIRECTION, "angle" : 43.5 * degree});
        }
        {
            var Q0;
            {var subQ0=sQuery(id+"F1.wireOp",EDGE,"E31.MirrorCS");var subQ1=sQuery(id+"F1.wireOp",EDGE,"E30.MirrorCS");var subQ2=makeQuery(id+"F1.imprint","INTERSECT",VERTEX,{"derivedFrom":[subQ1,subQ0]});Q0=makeQuery(id+"F1.imprint","IMPRINT",FACE,{"disambiguationData":[TD([[makeQuery(id+"F1.imprint","IMPRINT",EDGE,{"disambiguationData":[TD([[subQ2,1.0]])],"derivedFrom":subQ1}),-1.0]])]});}
            var Q1;
            Q1=sQuery(id+"F1.wireOp",EDGE,"E11");
            revolve(context, id + "F7", {"entities" : qUnion([Q0]), "axis" : qUnion([Q1]), "revolveType" : RevolveType.FULL});
        }
        {
            var Q0;
            Q0=makeQuery(id+"F4.opRevolve","SWEPT_EDGE",EDGE,{"disambiguationData":[OSD([sQuery(id+"F1.wireOp",EDGE,"E31.MirrorCS"),sQuery(id+"F1.wireOp",EDGE,"E139")])]});
            var Q1;
            Q1=makeQuery(id+"F4.opRevolve","SWEPT_FACE",FACE,{"disambiguationData":[OSD([sQuery(id+"F1.wireOp",EDGE,"E31.MirrorCS")])]});
            var Q2;
            Q2=makeQuery(id+"F5.opRevolve","SWEPT_FACE",FACE,{"disambiguationData":[OSD([sQuery(id+"F1.wireOp",EDGE,"E31.MirrorCS")])]});
            var Q3;
            Q3=makeQuery(id+"F6.opRevolve","SWEPT_FACE",FACE,{"disambiguationData":[OSD([sQuery(id+"F1.wireOp",EDGE,"E31.MirrorCS")])]});
            var Q4;
            Q4=makeQuery(id+"F7.opRevolve","SWEPT_FACE",FACE,{"disambiguationData":[OSD([sQuery(id+"F1.wireOp",EDGE,"E31.MirrorCS")])]});
            fillet(context, id + "F8", {"entities" : qUnion([Q0, Q1, Q2, Q3, Q4]), "radius" : 0.13 * mm, "allowEdgeOverflow" : false});
        }
        {
            var Q0;
            Q0=makeQuery(id+"F5.opRevolve","SWEPT_BODY",BODY,{"disambiguationData":[OSD([sQuery(id+"F1.wireOp",EDGE,"E31.MirrorCS"),sQuery(id+"F1.wireOp",EDGE,"E140.0"),sQuery(id+"F1.wireOp",EDGE,"E28.MirrorCS"),sQuery(id+"F1.wireOp",EDGE,"E139")])]});
            var Q1;
            Q1=makeQuery(id+"F6.opRevolve","SWEPT_BODY",BODY,{"disambiguationData":[OSD([sQuery(id+"F1.wireOp",EDGE,"E31.MirrorCS"),sQuery(id+"F1.wireOp",EDGE,"E140.0"),sQuery(id+"F1.wireOp",EDGE,"E29.MirrorCS"),sQuery(id+"F1.wireOp",EDGE,"E28.MirrorCS")])]});
            var Q2;
            Q2=sQuery(id+"F1.wireOp",EDGE,"E11");
            circularPattern(context, id + "F9", {"operationType" : NewBodyOperationType.ADD, "entities" : qUnion([Q0, Q1]), "axis" : qUnion([Q2]), "angle" : 360 * degree, "instanceCount" : 8, "equalSpace" : true});
        }
        {
            var Q0;
            {var subQ0=sQuery(id+"F0.wireOp",EDGE,"E5.right");Q0=makeQuery(id+"F0.imprint","IMPRINT",FACE,{"disambiguationData":[TD([[makeQuery(id+"F0.imprint","IMPRINT",EDGE,{"derivedFrom":subQ0}),-1.0]])]});}
            var Q1;
            {var subQ0=sQuery(id+"F0.wireOp",EDGE,"E5.left");Q1=makeQuery(id+"F0.imprint","IMPRINT",FACE,{"disambiguationData":[TD([[makeQuery(id+"F0.imprint","IMPRINT",EDGE,{"derivedFrom":subQ0}),1.0]])]});}
            var Q2;
            {var subQ0=sQuery(id+"F0.wireOp",EDGE,"E4.left");Q2=makeQuery(id+"F0.imprint","IMPRINT",FACE,{"disambiguationData":[TD([[makeQuery(id+"F0.imprint","IMPRINT",EDGE,{"derivedFrom":subQ0}),-1.0]])]});}
            var Q3;
            {var subQ0=sQuery(id+"F0.wireOp",EDGE,"E4.right");Q3=makeQuery(id+"F0.imprint","IMPRINT",FACE,{"disambiguationData":[TD([[makeQuery(id+"F0.imprint","IMPRINT",EDGE,{"derivedFrom":subQ0}),1.0]])]});}
            extrude(context, id + "F10", {"entities" : qUnion([Q0, Q1, Q2, Q3]), "operationType" : NewBodyOperationType.REMOVE, "oppositeDirection" : true, "depth" : 2.8 * mm});
        }
        {
            var Q0;
            Q0=makeQuery(id+"F1.imprint","IMPRINT",FACE,{"disambiguationData":[TD([[makeQuery(id+"F1.imprint","IMPRINT",EDGE,{"derivedFrom":sQuery(id+"F1.wireOp",EDGE,"E47.MirrorCS")}),1.0]])]});
            var Q1;
            Q1=makeQuery(id+"F1.imprint","IMPRINT",FACE,{"disambiguationData":[TD([[makeQuery(id+"F1.imprint","IMPRINT",EDGE,{"derivedFrom":sQuery(id+"F1.wireOp",EDGE,"E48.MirrorCS")}),1.0]])]});
            var Q2;
            Q2=makeQuery(id+"F1.imprint","IMPRINT",FACE,{"disambiguationData":[TD([[makeQuery(id+"F1.imprint","IMPRINT",EDGE,{"derivedFrom":sQuery(id+"F1.wireOp",EDGE,"E49.MirrorCS")}),1.0]])]});
            var Q3;
            {var subQ1=sQuery(id+"F1.wireOp",EDGE,"E15");Q3=makeQuery(id+"F1.imprint","IMPRINT",FACE,{"disambiguationData":[TD([[makeQuery(id+"F1.imprint","IMPRINT",EDGE,{"derivedFrom":subQ1}),1.0]])]});}
            var Q4;
            Q4=makeQuery(id+"F1.imprint","IMPRINT",FACE,{"disambiguationData":[TD([[makeQuery(id+"F1.imprint","IMPRINT",EDGE,{"derivedFrom":sQuery(id+"F1.wireOp",EDGE,"E20")}),-1.0]])]});
            var Q5;
            Q5=makeQuery(id+"F1.imprint","IMPRINT",FACE,{"disambiguationData":[TD([[makeQuery(id+"F1.imprint","IMPRINT",EDGE,{"derivedFrom":sQuery(id+"F1.wireOp",EDGE,"E19")}),-1.0]])]});
            var Q6;
            Q6=sQuery(id+"F1.wireOp",EDGE,"E17");
            revolve(context, id + "F11", {"operationType" : NewBodyOperationType.ADD, "entities" : qUnion([Q0, Q1, Q2, Q3, Q4, Q5]), "axis" : qUnion([Q6]), "revolveType" : RevolveType.SYMMETRIC, "angle" : 30 * degree});
        }
        {
            var Q0;
            Q0=makeQuery(id+"F11.opRevolve","SWEPT_EDGE",EDGE,{"disambiguationData":[OSD([sQuery(id+"F1.wireOp",EDGE,"E20"),sQuery(id+"F1.wireOp",EDGE,"E22"),sQuery(id+"F1.wireOp",EDGE,"E34")])]});
            var Q1;
            Q1=makeQuery(id+"F11.opRevolve","SWEPT_EDGE",EDGE,{"disambiguationData":[OSD([sQuery(id+"F1.wireOp",EDGE,"E48.MirrorCS"),sQuery(id+"F1.wireOp",EDGE,"E50.MirrorCS"),sQuery(id+"F1.wireOp",EDGE,"E51.MirrorCS")])]});
            fillet(context, id + "F12", {"entities" : qUnion([Q0, Q1]), "radius" : 0.38 * mm, "tangentPropagation" : true, "allowEdgeOverflow" : false});
        }
        {
            var Q0;
            Q0=makeQuery(id+"F11.opRevolve","SWEPT_EDGE",EDGE,{"disambiguationData":[OSD([sQuery(id+"F1.wireOp",EDGE,"E164.MirrorCS"),sQuery(id+"F1.wireOp",EDGE,"E166.MirrorCS")])]});
            var Q1;
            Q1=makeQuery(id+"F11.opRevolve","SWEPT_EDGE",EDGE,{"disambiguationData":[OSD([sQuery(id+"F1.wireOp",EDGE,"E18"),sQuery(id+"F1.wireOp",EDGE,"E53")])]});
            var Q2;
            {var subQ0=sQuery(id+"F1.wireOp",EDGE,"E143");var subQ1=sQuery(id+"F1.wireOp",EDGE,"E159.MirrorCS");var subQ2=sQuery(id+"F1.wireOp",EDGE,"E153");var subQ3=sQuery(id+"F1.wireOp",EDGE,"E145");Q2=makeQuery(id+"F11.boolean.opBoolean","SPLIT",EDGE,{"disambiguationData":[TD([makeQuery(id+"F11.opRevolve","CAP_FACE",FACE,{"disambiguationData":[OSD([sQuery(id+"F1.wireOp",EDGE,"E47.MirrorCS"),sQuery(id+"F1.wireOp",EDGE,"E50.MirrorCS"),sQuery(id+"F1.wireOp",EDGE,"E51.MirrorCS"),sQuery(id+"F1.wireOp",EDGE,"E157.MirrorCS"),subQ1,sQuery(id+"F1.wireOp",EDGE,"E160.MirrorCS"),sQuery(id+"F1.wireOp",EDGE,"E163.MirrorCS"),sQuery(id+"F1.wireOp",EDGE,"E164.MirrorCS"),sQuery(id+"F1.wireOp",EDGE,"E165.MirrorCS"),sQuery(id+"F1.wireOp",EDGE,"E158.MirrorCS"),sQuery(id+"F1.wireOp",EDGE,"E166.MirrorCS"),sQuery(id+"F1.wireOp",EDGE,"E168.MirrorCS"),sQuery(id+"F1.wireOp",EDGE,"E167.MirrorCS"),sQuery(id+"F1.wireOp",EDGE,"E162.MirrorCS"),sQuery(id+"F1.wireOp",EDGE,"E173"),sQuery(id+"F1.wireOp",EDGE,"E175")])],"isStart":true})])],"derivedFrom":makeQuery(id+"F3.opRevolve","SWEPT_EDGE",EDGE,{"disambiguationData":[OSD([subQ0,subQ3,subQ2])]})});}
            var Q3;
            {var subQ0=sQuery(id+"F1.wireOp",EDGE,"E144.MirrorCS");var subQ1=sQuery(id+"F1.wireOp",EDGE,"E153");var subQ2=sQuery(id+"F1.wireOp",EDGE,"E160.MirrorCS");var subQ3=sQuery(id+"F1.wireOp",EDGE,"E146");Q3=makeQuery(id+"F11.boolean.opBoolean","SPLIT",EDGE,{"disambiguationData":[TD([makeQuery(id+"F11.opRevolve","CAP_FACE",FACE,{"disambiguationData":[OSD([sQuery(id+"F1.wireOp",EDGE,"E47.MirrorCS"),sQuery(id+"F1.wireOp",EDGE,"E50.MirrorCS"),sQuery(id+"F1.wireOp",EDGE,"E51.MirrorCS"),sQuery(id+"F1.wireOp",EDGE,"E157.MirrorCS"),sQuery(id+"F1.wireOp",EDGE,"E159.MirrorCS"),subQ2,sQuery(id+"F1.wireOp",EDGE,"E163.MirrorCS"),sQuery(id+"F1.wireOp",EDGE,"E164.MirrorCS"),sQuery(id+"F1.wireOp",EDGE,"E165.MirrorCS"),sQuery(id+"F1.wireOp",EDGE,"E158.MirrorCS"),sQuery(id+"F1.wireOp",EDGE,"E166.MirrorCS"),sQuery(id+"F1.wireOp",EDGE,"E168.MirrorCS"),sQuery(id+"F1.wireOp",EDGE,"E167.MirrorCS"),sQuery(id+"F1.wireOp",EDGE,"E162.MirrorCS"),sQuery(id+"F1.wireOp",EDGE,"E173"),sQuery(id+"F1.wireOp",EDGE,"E175")])],"isStart":true})])],"derivedFrom":makeQuery(id+"F3.opRevolve","SWEPT_EDGE",EDGE,{"disambiguationData":[OSD([subQ0,subQ3,subQ1])]})});}
            var Q4;
            Q4=makeQuery(id+"F11.opRevolve","CAP_EDGE",EDGE,{"disambiguationData":[OSD([sQuery(id+"F1.wireOp",EDGE,"E15")]),OD(0.0)],"isStart":false});
            var Q5;
            Q5=makeQuery(id+"F11.opRevolve","CAP_EDGE",EDGE,{"disambiguationData":[OSD([sQuery(id+"F1.wireOp",EDGE,"E16")]),OD(0.0)],"isStart":false});
            var Q6;
            Q6=makeQuery(id+"F11.opRevolve","CAP_EDGE",EDGE,{"disambiguationData":[OSD([sQuery(id+"F1.wireOp",EDGE,"E167.MirrorCS")])],"isStart":true});
            var Q7;
            Q7=makeQuery(id+"F11.opRevolve","CAP_EDGE",EDGE,{"disambiguationData":[OSD([sQuery(id+"F1.wireOp",EDGE,"E16")]),OD(1.0)],"isStart":false});
            var Q8;
            Q8=makeQuery(id+"F11.opRevolve","CAP_EDGE",EDGE,{"disambiguationData":[OSD([sQuery(id+"F1.wireOp",EDGE,"E167.MirrorCS")])],"isStart":false});
            fillet(context, id + "F13", {"entities" : qUnion([Q0, Q1, Q2, Q3, Q4, Q5, Q6, Q7, Q8]), "radius" : 0.08 * mm, "tangentPropagation" : true, "allowEdgeOverflow" : false});
        }
    });
